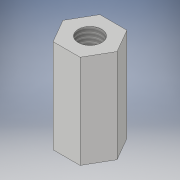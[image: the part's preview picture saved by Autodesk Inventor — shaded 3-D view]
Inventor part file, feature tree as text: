
AUTODESK INVENTOR PART (.ipt)
format: ipt  version: 2017.3 (Build 213257000, 257)  size: 102,912 bytes
history: native  units: mm
features: sketch x2, extrude x1, hole x1, thread x1
ambient origin geometry x8: Origin, YZ Plane, XZ Plane, XY Plane, X Axis, Y Axis, Z Axis, Center Point
bodies: Volumenkörper1 (feature_tree)
feature tree (5):
  extrude  "Extrusion1"  TaperAngle=120.0deg  [1 undecoded]
  hole  "Bohrung1"  [1 undecoded]
  thread  "Gewinde1"  [1 undecoded]
  sketch  "Skizze1"  dims[d3=120.0deg d4=120.0deg]
  sketch  "Skizze2"  dims[d5=120.0deg d6=5.0mm d7=10.0mm d8=0.0mm d9=2.5mm d10=5.0mm d11=4.0mm d12=2.0mm d13=90.0deg d14=7.6mm d15=20.594885mm d16=10.0mm d17=0.0mm]
note: 3 required parameter values undecoded (feature->parameter linkage not recoverable at this tier; creation-order binding heuristic only, values carry confidence <= 0.55)
